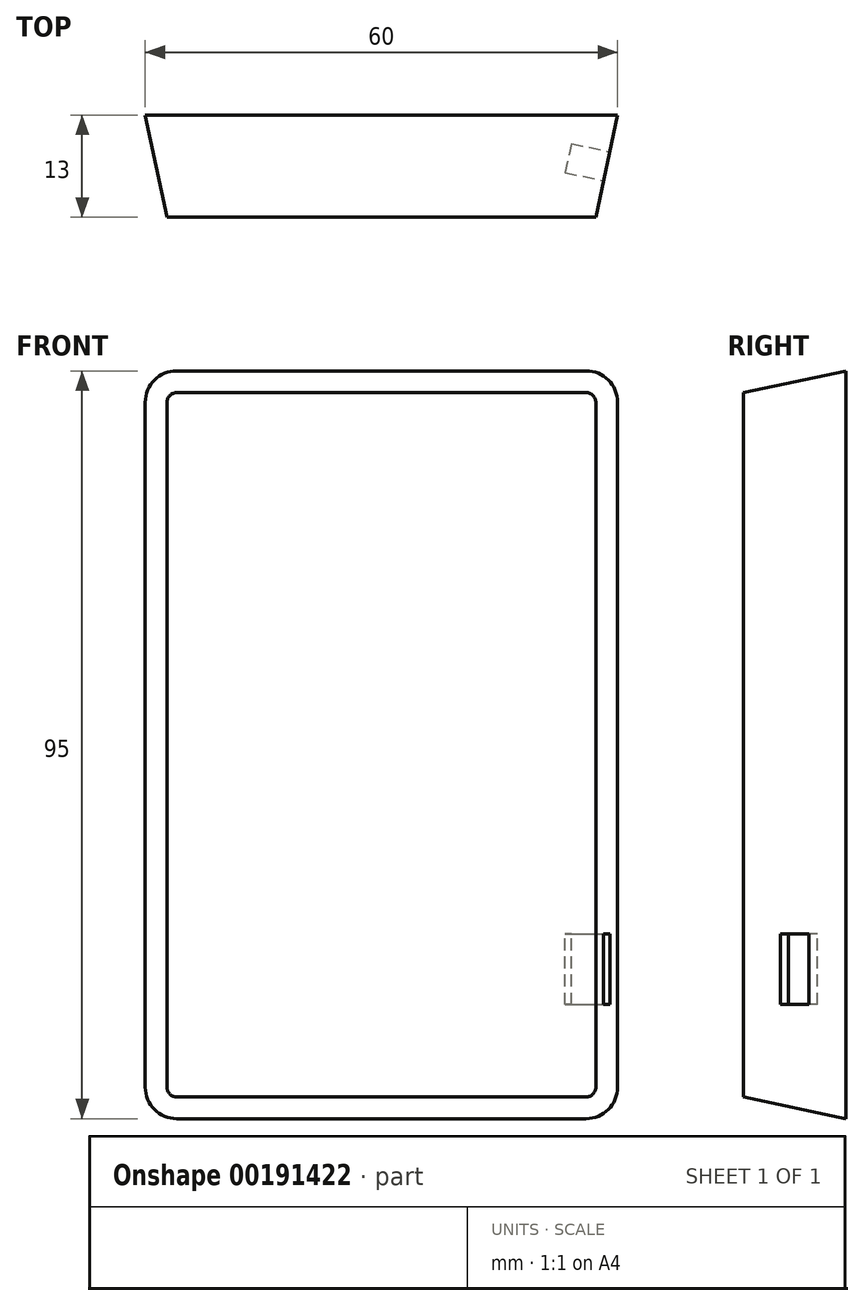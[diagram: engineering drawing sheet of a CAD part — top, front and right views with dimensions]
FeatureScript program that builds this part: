
annotation { "Feature Type Name" : "Feature", "Feature Type Description" : "" }
export const myFeature = defineFeature(function(context is Context, id is Id, definition is map)
    precondition{}
    {
        {
            var Q0;
            Q0=qCreatedBy(makeId("Front.planeOp"),FACE);
            var sketch = newSketch(context, id + "F0", { "sketchPlane" : qUnion([Q0])});
            skLineSegment(sketch, "E0.bottom", {"start": v(4, 0) * mm, "end": v(56, 0) * mm});
            skLineSegment(sketch, "E0.top", {"start": v(4, 95) * mm, "end": v(56, 95) * mm});
            skLineSegment(sketch, "E0.left", {"start": v(0, 4) * mm, "end": v(0, 91) * mm});
            skLineSegment(sketch, "E0.right", {"start": v(60, 4) * mm, "end": v(60, 91) * mm});
            skPoint(sketch, "E1.visualSharp", {"position": v(60, 95) * mm});
            skArc(sketch, "E1.filletArc", {"start": v(60, 91) * mm, "mid": v(58.83, 93.83) * mm, "end": v(56, 95) * mm});
            skPoint(sketch, "E2.visualSharp", {"position": v(60, 0) * mm});
            skArc(sketch, "E2.filletArc", {"start": v(56, 0) * mm, "mid": v(58.83, 1.17) * mm, "end": v(60, 4) * mm});
            skPoint(sketch, "E3.visualSharp", {"position": v(0, 0) * mm});
            skArc(sketch, "E3.filletArc", {"start": v(0, 4) * mm, "mid": v(1.17, 1.17) * mm, "end": v(4, 0) * mm});
            skPoint(sketch, "E4.visualSharp", {"position": v(0, 95) * mm});
            skArc(sketch, "E4.filletArc", {"start": v(4, 95) * mm, "mid": v(1.17, 93.83) * mm, "end": v(0, 91) * mm});
            skSolve(sketch);
        }
        {
            var Q0;
            Q0=makeQuery(id+"F0.imprint","IMPRINT",FACE,{"disambiguationData":[TD([[makeQuery(id+"F0.imprint","IMPRINT",EDGE,{"derivedFrom":sQuery(id+"F0.wireOp",EDGE,"E0.bottom")}),1.0]])]});
            extrude(context, id + "F3", {"entities" : qUnion([Q0]), "depth" : 13 * mm, "hasDraft" : true, "draftAngle" : 12 * degree, "draftPullDirection" : true});
        }
        {
            var Q0;
            Q0=makeQuery(id+"F3.opExtrude","SWEPT_FACE",FACE,{"disambiguationData":[OSD([sQuery(id+"F0.wireOp",EDGE,"E0.right")])]});
            var sketch = newSketch(context, id + "F1", { "sketchPlane" : qUnion([Q0])});
            skLineSegment(sketch, "E5", {"start": v(5.83, 91) * mm, "end": v(5.83, 4) * mm, "construction": true});
            skLineSegment(sketch, "E6.bottom", {"start": v(7.7, 14.5) * mm, "end": v(3.95, 14.5) * mm});
            skLineSegment(sketch, "E6.top", {"start": v(7.7, 23.5) * mm, "end": v(3.95, 23.5) * mm});
            skLineSegment(sketch, "E6.left", {"start": v(7.7, 14.5) * mm, "end": v(7.7, 23.5) * mm});
            skLineSegment(sketch, "E6.right", {"start": v(3.95, 14.5) * mm, "end": v(3.95, 23.5) * mm});
            skPoint(sketch, "E6.middle", {"position": v(5.83, 19) * mm});
            skSolve(sketch);
        }
        {
            var Q0;
            Q0 = qSketchRegion(id + "F1", true);
            extrude(context, id + "F2", {"entities" : qUnion([Q0]), "operationType" : NewBodyOperationType.REMOVE, "oppositeDirection" : true, "depth" : 5 * mm});
        }
    });
